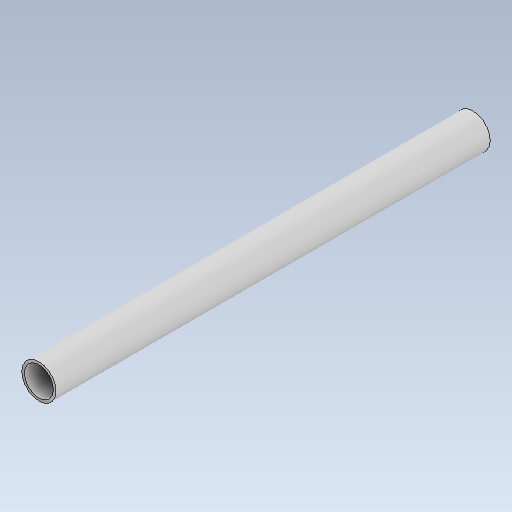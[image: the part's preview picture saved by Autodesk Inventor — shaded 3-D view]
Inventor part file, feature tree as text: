
AUTODESK INVENTOR PART (.ipt)
format: ipt  version: 2020 (Build 240168000, 168)  size: 119,296 bytes
history: native  units: mm
features: extrude x1, sketch x1
ambient origin geometry x8: Origin, YZ Plane, XZ Plane, XY Plane, X Axis, Y Axis, Z Axis, Center Point
bodies: Solid1 (feature_tree)
feature tree (2):
  extrude  "Extrusion1"  Depth=165.196764mm
  sketch  "Sketch1"  dims[d0=11.0mm d1=13.0mm d2=165.196764mm d3=0.0mm]
